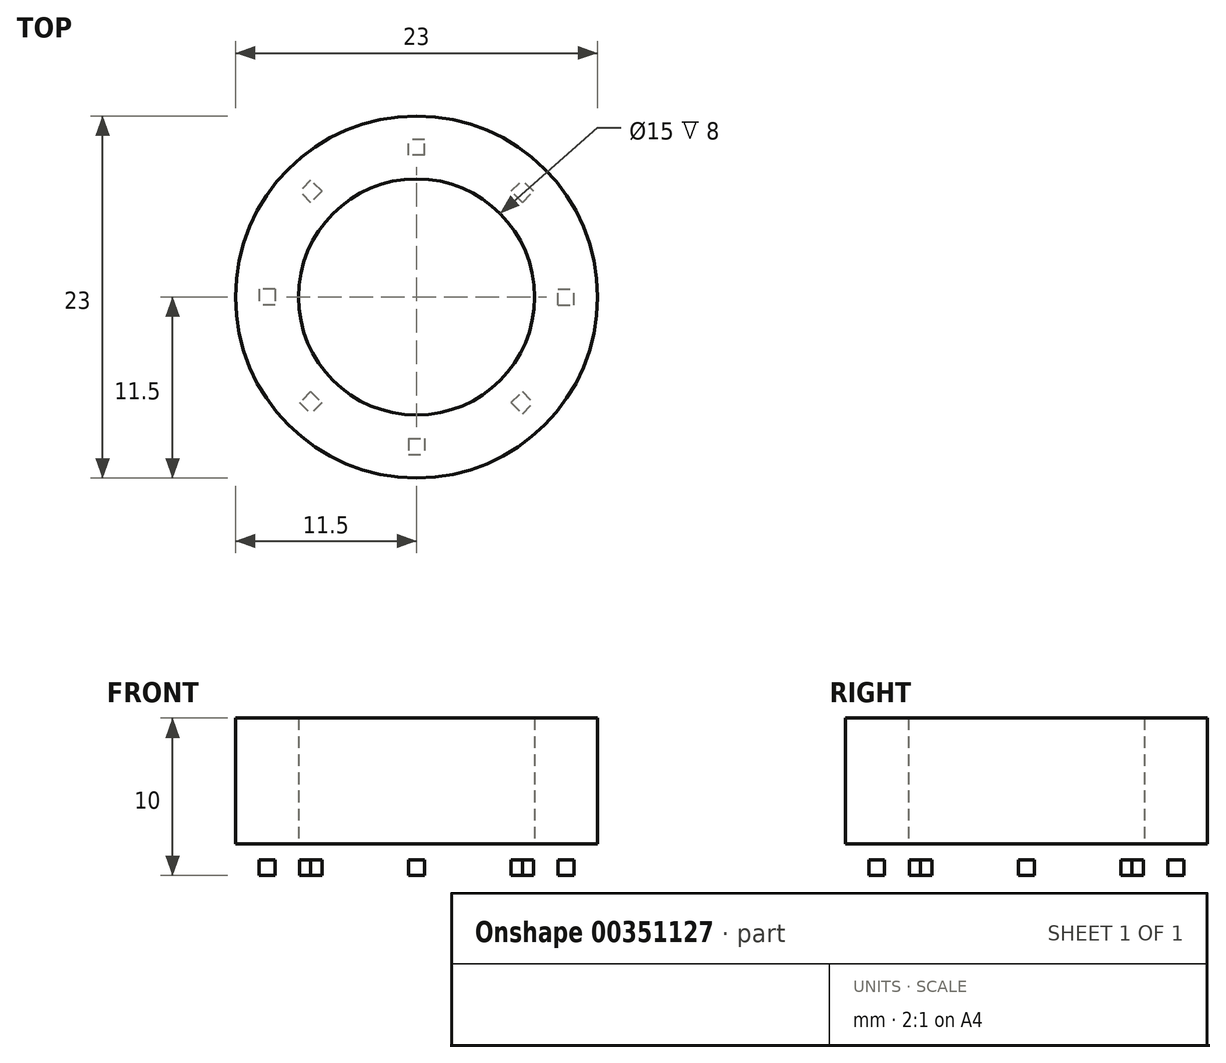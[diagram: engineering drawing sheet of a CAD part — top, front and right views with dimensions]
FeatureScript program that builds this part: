
annotation { "Feature Type Name" : "Feature", "Feature Type Description" : "" }
export const myFeature = defineFeature(function(context is Context, id is Id, definition is map)
    precondition{}
    {
        {
            var Q0;
            Q0=qCreatedBy(makeId("Right.planeOp"),FACE);
            var sketch = newSketch(context, id + "F0", { "sketchPlane" : qUnion([Q0])});
            skLineSegment(sketch, "E0.bottom", {"start": v(9, -1) * mm, "end": v(10, -1) * mm});
            skLineSegment(sketch, "E0.top", {"start": v(9, -2) * mm, "end": v(10, -2) * mm});
            skLineSegment(sketch, "E0.left", {"start": v(9, -1) * mm, "end": v(9, -2) * mm});
            skLineSegment(sketch, "E0.right", {"start": v(10, -1) * mm, "end": v(10, -2) * mm});
            skLineSegment(sketch, "E1", {"start": v(0, -10.63) * mm, "end": v(0, 13.77) * mm});
            skSolve(sketch);
        }
        {
            var Q0;
            Q0=makeQuery(id+"F0.imprint","IMPRINT",FACE,{"disambiguationData":[TD([[makeQuery(id+"F0.imprint","IMPRINT",EDGE,{"derivedFrom":sQuery(id+"F0.wireOp",EDGE,"E0.bottom")}),-1.0]])]});
            extrude(context, id + "F1", {"entities" : qUnion([Q0]), "endBound" : BoundingType.SYMMETRIC, "depth" : 1 * mm});
        }
        {
            var Q0;
            Q0=makeQuery(id+"F1.opExtrude","SWEPT_BODY",BODY,{"disambiguationData":[OSD([sQuery(id+"F0.wireOp",EDGE,"E0.bottom"),sQuery(id+"F0.wireOp",EDGE,"E0.top"),sQuery(id+"F0.wireOp",EDGE,"E0.left"),sQuery(id+"F0.wireOp",EDGE,"E0.right")])]});
            var Q1;
            Q1=sQuery(id+"F0.wireOp",EDGE,"E1");
            circularPattern(context, id + "F2", {"entities" : qUnion([Q0]), "axis" : qUnion([Q1]), "angle" : 360 * degree, "instanceCount" : 8, "oppositeDirection" : true, "equalSpace" : true});
        }
        {
            var Q0;
            Q0=qCreatedBy(makeId("Top.planeOp"),FACE);
            var sketch = newSketch(context, id + "F3", { "sketchPlane" : qUnion([Q0])});
            skCircle(sketch, "E2", {"center": v(0, 0) * mm, "radius": 7.5 * mm});
            skCircle(sketch, "E3.0", {"center": v(0, 0) * mm, "radius": 11.5 * mm});
            skSolve(sketch);
        }
        {
            var Q0;
            Q0=makeQuery(id+"F3.imprint","IMPRINT",FACE,{"disambiguationData":[TD([[makeQuery(id+"F3.imprint","IMPRINT",EDGE,{"derivedFrom":sQuery(id+"F3.wireOp",EDGE,"E2")}),-1.0]])]});
            extrude(context, id + "F4", {"entities" : qUnion([Q0]), "depth" : 8 * mm});
        }
    });
